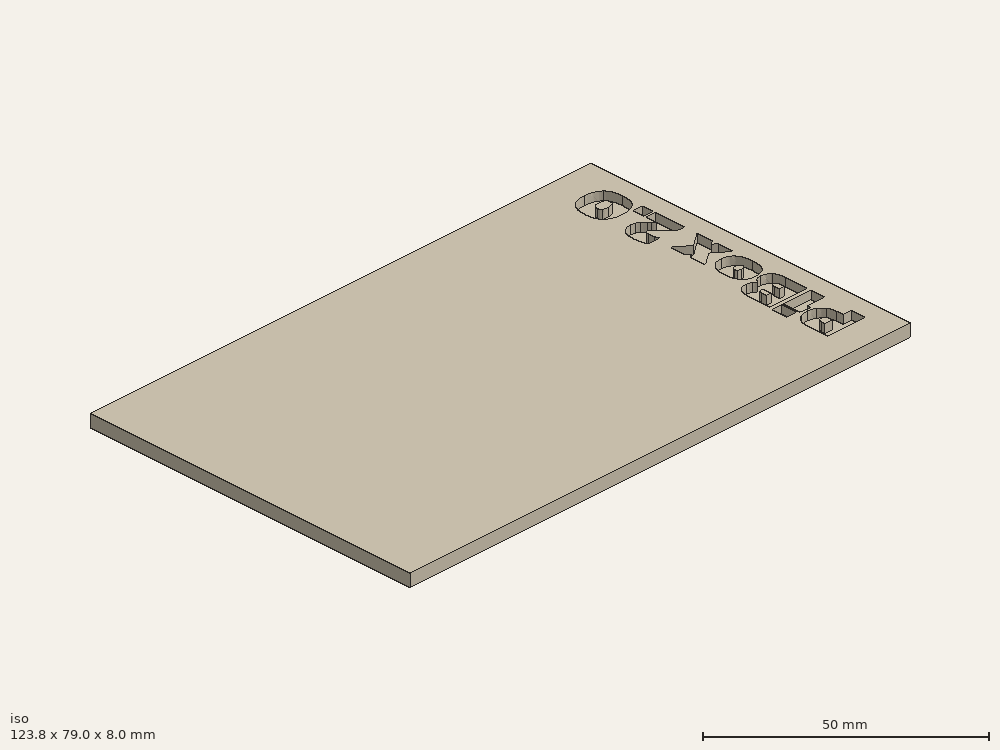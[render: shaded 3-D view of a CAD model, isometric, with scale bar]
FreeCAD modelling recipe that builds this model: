
FCSTD DOCUMENT  (FreeCAD 0.19R24267 +148 (Git))
Label: top_cover_logo
License: All rights reserved
LicenseURL: http://en.wikipedia.org/wiki/All_rights_reserved
objects: Part::Feature×1, Part::Part2DObjectPython×1, Part::Extrusion×1, Part::Cut×1
note: 4 computed .brp shape members not serialized (recipe doc carries the construction recipe); baked Part::Feature solids carry a one-line shape summary decoded from their .brp

FEATURE [Part::Feature] top_cover001001_solid  label="top_cover001001 (Solid)"
  shape: bbox 123.8 x 79 x 8 mm, 7846 faces (baked)
FEATURE [Part::Part2DObjectPython] ShapeString  # Draft 2D object (typed FeaturePython)
  FontFile = <userpath>/Desktop/pibox2.0/Kanit-Black.ttf
  Placement = pos=(60.69,-33.11,7) rot=(0,0,1;1.5708rad)
  Size = 7
  String = PiBox 2.0
  Tracking = 0
FEATURE [Part::Extrusion] Extrude
  Base = -> ShapeString
  Dir = (0,0,1)
  DirMode = 2
  FaceMakerClass = Part::FaceMakerBullseye
  LengthFwd = 2
  LengthRev = 0
  Placement = pos=(-3,0,-6) rot=(0,0,1;0rad)
  Solid = false
  Symmetric = false
FEATURE [Part::Cut] Cut
  Base = -> top_cover001001_solid
  Tool = -> Extrude
